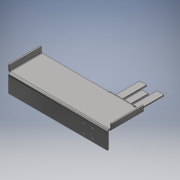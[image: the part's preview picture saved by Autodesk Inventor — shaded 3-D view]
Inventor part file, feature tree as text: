
AUTODESK INVENTOR PART (.ipt)
format: ipt  version: 2018 (Build 220112000, 112)  size: 223,232 bytes
history: native  units: mm
features: other x24, sketch x7, reference x4, hole x1
ambient origin geometry x8: Origin, YZ Plane, XZ Plane, XY Plane, X Axis, Y Axis, Z Axis, Center Point
bodies: Solido1 (feature_tree)
feature tree (36):
  other  "Faccia1"
  other  "Flangia1"
  other  "Flangia2"
  other  "Flangia3"
  other  "Flangia4"
  hole  "Foro1"  [1 undecoded]
  other  "Arrotondamento angolo1"
  sketch  "Schizzo1"
  other  "Piano1"
  sketch  "Schizzo2"
  other  "Piano2"
  other  "Piega (Bend)1"
  other  "Angolo1"
  sketch  "Schizzo3"
  other  "Piano3"
  other  "Piega (Bend)2"
  other  "Angolo2"
  sketch  "Schizzo4"
  other  "Piano4"
  other  "Piega (Bend)3"
  other  "Angolo3"
  sketch  "Schizzo5"
  other  "Piano5"
  other  "Piega (Bend)4"
  other  "Angolo4"
  sketch  "Schizzo6"
  sketch  "Schizzo7"
  reference  "Riferimento1"
  reference  "Riferimento2"
  reference  "Riferimento3"
  reference  "Riferimento4"
  other  "Taglia1"
  other  "<userpath>\no-brim\Meccanica\Progetto Inventor no-brim\Assiemi\Assieme 2 - Taglio.iam"
  other  "Assieme 2 - Taglio.iam"
  other  "536288 ADN-40-100-I-P-A---(0):1"
  other  "536288 ADN-100-P---(Z):1"
note: 1 required parameter value undecoded (feature->parameter linkage not recoverable at this tier; creation-order binding heuristic only, values carry confidence <= 0.55)
